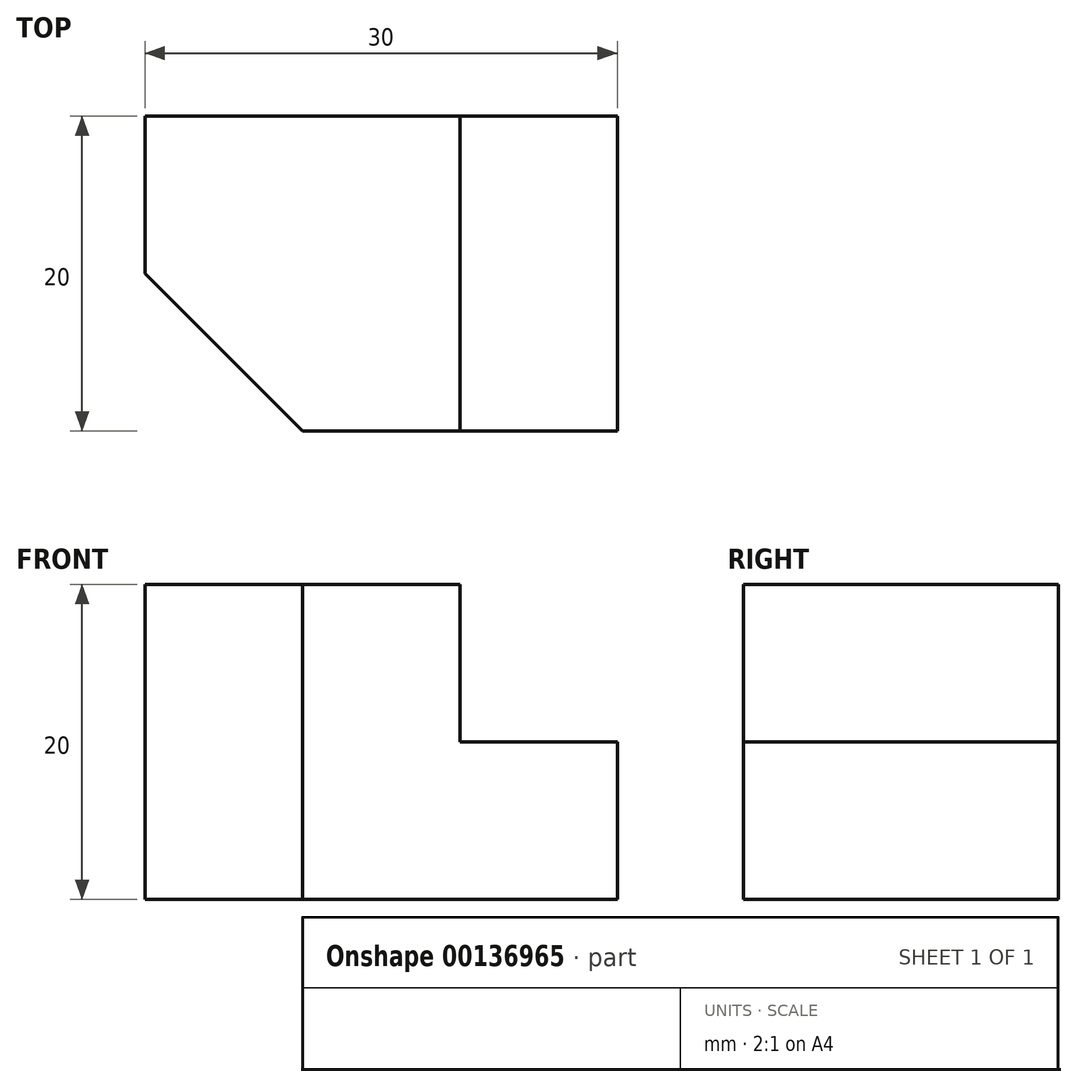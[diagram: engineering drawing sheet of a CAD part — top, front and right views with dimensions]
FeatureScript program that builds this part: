
annotation { "Feature Type Name" : "Feature", "Feature Type Description" : "" }
export const myFeature = defineFeature(function(context is Context, id is Id, definition is map)
    precondition{}
    {
        {
            var Q0;
            Q0=qCreatedBy(makeId("Top.planeOp"),FACE);
            var sketch = newSketch(context, id + "F0", { "sketchPlane" : qUnion([Q0])});
            skLineSegment(sketch, "E0", {"start": v(0, 20) * mm, "end": v(0, 10) * mm});
            skLineSegment(sketch, "E1", {"start": v(0, 10) * mm, "end": v(10, 0) * mm});
            skLineSegment(sketch, "E2", {"start": v(10, 0) * mm, "end": v(30, 0) * mm});
            skLineSegment(sketch, "E3", {"start": v(30, 0) * mm, "end": v(30, 20) * mm});
            skLineSegment(sketch, "E4", {"start": v(30, 20) * mm, "end": v(0, 20) * mm});
            skSolve(sketch);
        }
        {
            var Q0;
            Q0 = qSketchRegion(id + "F0", true);
            extrude(context, id + "F1", {"entities" : qUnion([Q0]), "depth" : 20 * mm});
        }
        {
            var Q0;
            Q0=makeQuery(id+"F1.opExtrude","SWEPT_FACE",FACE,{"disambiguationData":[OSD([sQuery(id+"F0.wireOp",EDGE,"E2")])]});
            var sketch = newSketch(context, id + "F2", { "sketchPlane" : qUnion([Q0])});
            skLineSegment(sketch, "E5", {"start": v(20, 20) * mm, "end": v(20, 10) * mm});
            skLineSegment(sketch, "E6", {"start": v(20, 10) * mm, "end": v(30, 10) * mm});
            skLineSegment(sketch, "E7", {"start": v(30, 10) * mm, "end": v(30, 20) * mm});
            skLineSegment(sketch, "E8", {"start": v(30, 20) * mm, "end": v(20, 20) * mm});
            skSolve(sketch);
        }
        {
            var Q0;
            Q0 = qSketchRegion(id + "F2", true);
            extrude(context, id + "F3", {"entities" : qUnion([Q0]), "operationType" : NewBodyOperationType.REMOVE, "endBound" : BoundingType.THROUGH_ALL, "oppositeDirection" : true, "depth" : 25 * mm});
        }
    });
